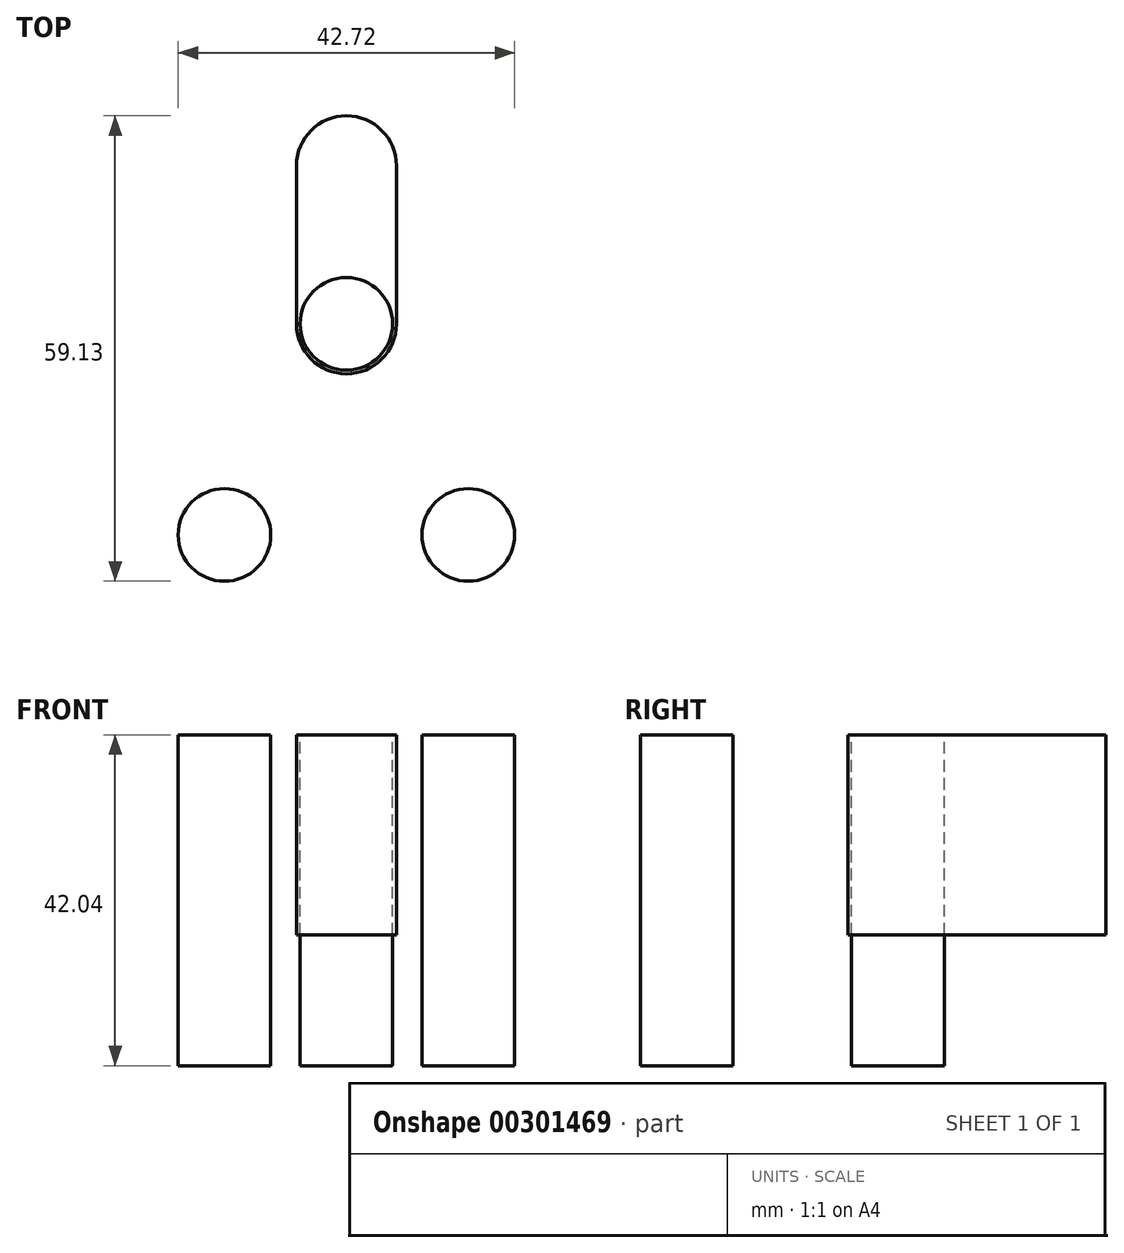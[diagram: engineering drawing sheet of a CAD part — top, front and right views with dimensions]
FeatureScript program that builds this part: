
annotation { "Feature Type Name" : "Feature", "Feature Type Description" : "" }
export const myFeature = defineFeature(function(context is Context, id is Id, definition is map)
    precondition{}
    {
        {
            var Q0;
            Q0=qCreatedBy(makeId("Top.planeOp"),FACE);
            var sketch = newSketch(context, id + "F0", { "sketchPlane" : qUnion([Q0])});
            skCircle(sketch, "E0", {"center": v(0, 0) * mm, "radius": 54.13 * mm});
            skSolve(sketch);
        }
        {
            var Q0;
            Q0 = qSketchRegion(id + "F0", true);
            extrude(context, id + "F1", {"entities" : qUnion([Q0]), "depth" : 25.4 * mm});
        }
        {
            var Q0;
            Q0=makeQuery(id+"F1.opExtrude","CAP_FACE",FACE,{"disambiguationData":[OSD([sQuery(id+"F0.wireOp",EDGE,"E0")])],"isStart":false});
            var sketch = newSketch(context, id + "F2", { "sketchPlane" : qUnion([Q0])});
            skLineSegment(sketch, "E1", {"start": v(0, 37.96) * mm, "end": v(0, 17.88) * mm});
            skArc(sketch, "E2.0.startCap", {"start": v(-6.35, 37.96) * mm, "mid": v(0, 44.31) * mm, "end": v(6.35, 37.96) * mm});
            skArc(sketch, "E2.0.endCap", {"start": v(6.35, 17.88) * mm, "mid": v(0, 11.53) * mm, "end": v(-6.35, 17.88) * mm});
            skLineSegment(sketch, "E2.0.left", {"start": v(6.35, 37.96) * mm, "end": v(6.35, 17.88) * mm});
            skLineSegment(sketch, "E2.0.right", {"start": v(-6.35, 37.96) * mm, "end": v(-6.35, 17.88) * mm});
            skLineSegment(sketch, "E3.1.0", {"start": v(-29.7, -24.48) * mm, "end": v(-12.3, -14.44) * mm});
            skArc(sketch, "E3.1.1", {"start": v(-18.66, -3.44) * mm, "mid": v(-9.98, -5.76) * mm, "end": v(-12.3, -14.44) * mm});
            skArc(sketch, "E3.1.2", {"start": v(-29.7, -24.48) * mm, "mid": v(-38.38, -22.16) * mm, "end": v(-36.05, -13.48) * mm});
            skLineSegment(sketch, "E3.1.3", {"start": v(-36.05, -13.48) * mm, "end": v(-18.66, -3.44) * mm});
            skLineSegment(sketch, "E3.2.0", {"start": v(36.05, -13.48) * mm, "end": v(18.66, -3.44) * mm});
            skArc(sketch, "E3.2.1", {"start": v(12.3, -14.44) * mm, "mid": v(9.98, -5.76) * mm, "end": v(18.66, -3.44) * mm});
            skArc(sketch, "E3.2.2", {"start": v(36.05, -13.48) * mm, "mid": v(38.38, -22.16) * mm, "end": v(29.7, -24.48) * mm});
            skLineSegment(sketch, "E3.2.3", {"start": v(29.7, -24.48) * mm, "end": v(12.3, -14.44) * mm});
            skPoint(sketch, "E3.center", {"position": v(0, 0) * mm});
            skSolve(sketch);
        }
        {
            var Q0;
            Q0=makeQuery(id+"F2.imprint","IMPRINT",FACE,{"disambiguationData":[TD([[makeQuery(id+"F2.imprint","IMPRINT",EDGE,{"derivedFrom":sQuery(id+"F2.wireOp",EDGE,"E3.1.0")}),1.0]])]});
            var Q1;
            Q1=makeQuery(id+"F2.imprint","IMPRINT",FACE,{"disambiguationData":[TD([[makeQuery(id+"F2.imprint","IMPRINT",EDGE,{"derivedFrom":sQuery(id+"F2.wireOp",EDGE,"E2.0.startCap")}),-1.0]])]});
            var Q2;
            Q2=makeQuery(id+"F2.imprint","IMPRINT",FACE,{"disambiguationData":[TD([[makeQuery(id+"F2.imprint","IMPRINT",EDGE,{"derivedFrom":sQuery(id+"F2.wireOp",EDGE,"E3.2.0")}),1.0]])]});
            extrude(context, id + "F3", {"entities" : qUnion([Q0, Q1, Q2]), "operationType" : NewBodyOperationType.REMOVE, "endBound" : BoundingType.THROUGH_ALL, "oppositeDirection" : true, "depth" : 25.4 * mm});
        }
        {
            var Q0;
            Q0=makeQuery(id+"F1.opExtrude","CAP_FACE",FACE,{"disambiguationData":[OSD([sQuery(id+"F0.wireOp",EDGE,"E0")])],"isStart":false});
            var sketch = newSketch(context, id + "F4", { "sketchPlane" : qUnion([Q0])});
            skCircle(sketch, "E4", {"center": v(0, 17.88) * mm, "radius": 5.88 * mm});
            skCircle(sketch, "E5.1.0", {"center": v(-15.48, -8.94) * mm, "radius": 5.88 * mm});
            skCircle(sketch, "E5.2.0", {"center": v(15.48, -8.94) * mm, "radius": 5.88 * mm});
            skPoint(sketch, "E5.center", {"position": v(0, 0) * mm});
            skSolve(sketch);
        }
        {
            var Q0;
            Q0=makeQuery(id+"F4.imprint","IMPRINT",FACE,{"disambiguationData":[TD([[makeQuery(id+"F4.imprint","IMPRINT",EDGE,{"derivedFrom":sQuery(id+"F4.wireOp",EDGE,"E5.1.0")}),1.0]])]});
            var Q1;
            Q1=makeQuery(id+"F4.imprint","IMPRINT",FACE,{"disambiguationData":[TD([[makeQuery(id+"F4.imprint","IMPRINT",EDGE,{"derivedFrom":sQuery(id+"F4.wireOp",EDGE,"E5.2.0")}),1.0]])]});
            var Q2;
            Q2=makeQuery(id+"F4.imprint","IMPRINT",FACE,{"disambiguationData":[TD([[makeQuery(id+"F4.imprint","IMPRINT",EDGE,{"derivedFrom":sQuery(id+"F4.wireOp",EDGE,"E4")}),1.0]])]});
            extrude(context, id + "F5", {"entities" : qUnion([Q0, Q1, Q2]), "oppositeDirection" : true, "depth" : 42.04 * mm});
        }
    });
